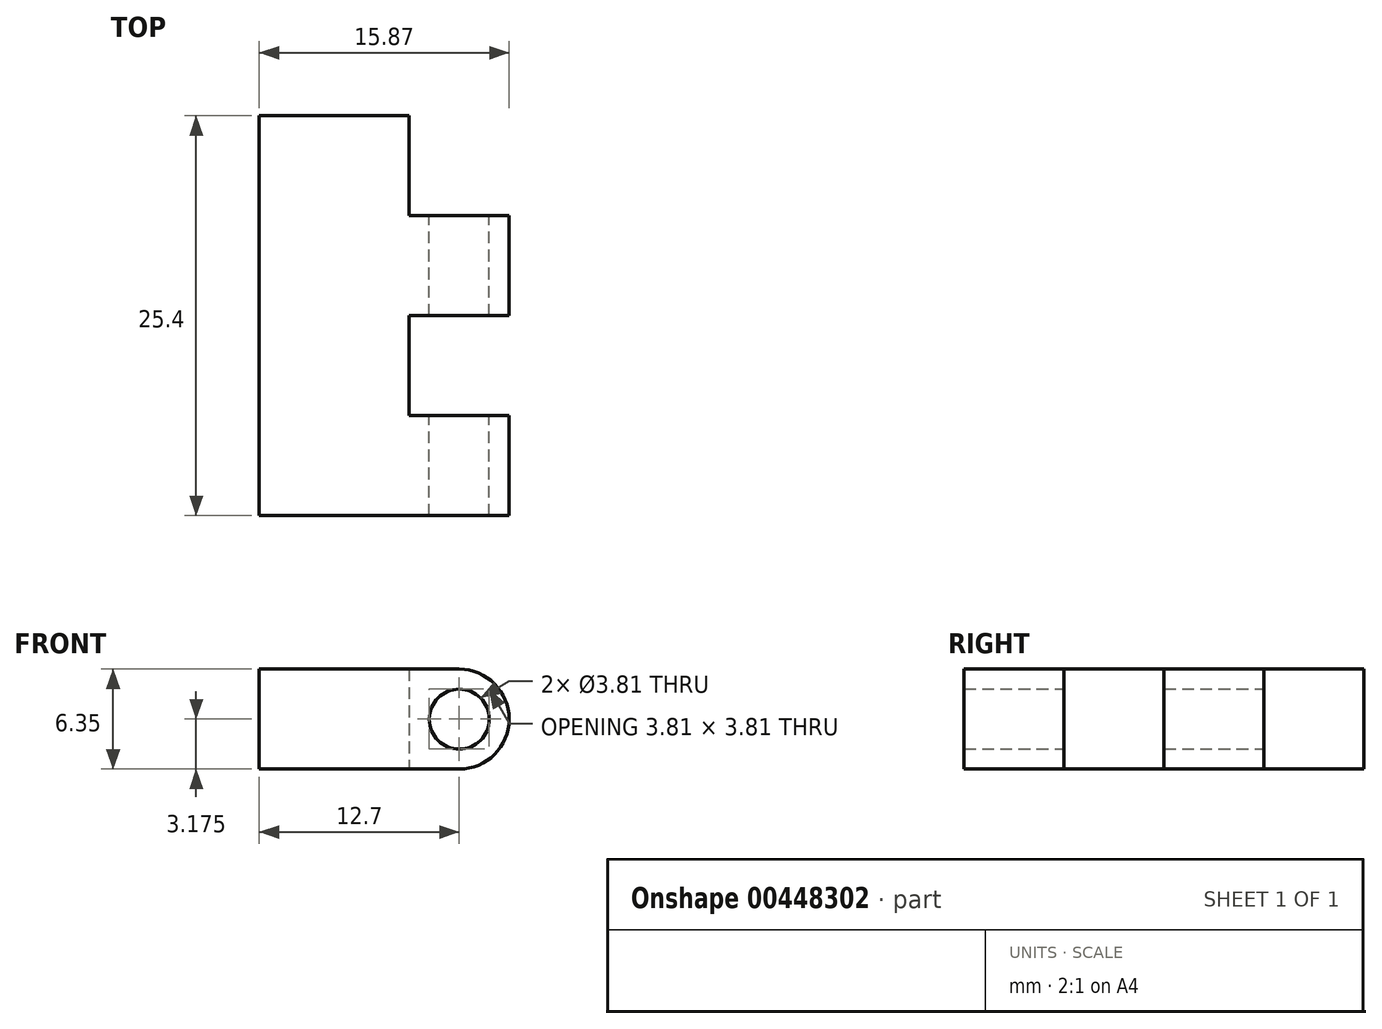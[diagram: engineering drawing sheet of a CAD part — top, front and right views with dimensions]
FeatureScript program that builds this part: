
annotation { "Feature Type Name" : "Feature", "Feature Type Description" : "" }
export const myFeature = defineFeature(function(context is Context, id is Id, definition is map)
    precondition{}
    {
        {
            var Q0;
            Q0=qCreatedBy(makeId("Top.planeOp"),FACE);
            var sketch = newSketch(context, id + "F0", { "sketchPlane" : qUnion([Q0])});
            skLineSegment(sketch, "E0.bottom", {"start": v(6.35, -12.7) * mm, "end": v(-6.35, -12.7) * mm});
            skLineSegment(sketch, "E0.top", {"start": v(6.35, 12.7) * mm, "end": v(-6.35, 12.7) * mm});
            skLineSegment(sketch, "E0.left", {"start": v(6.35, -12.7) * mm, "end": v(6.35, 12.7) * mm});
            skLineSegment(sketch, "E0.right", {"start": v(-6.35, -12.7) * mm, "end": v(-6.35, 12.7) * mm});
            skPoint(sketch, "E0.middle", {"position": v(0, 0) * mm});
            skSolve(sketch);
        }
        {
            var Q0;
            Q0 = qSketchRegion(id + "F0", true);
            extrude(context, id + "F1", {"entities" : qUnion([Q0]), "depth" : 6.35 * mm});
        }
        {
            var Q0;
            Q0=makeQuery(id+"F1.opExtrude","SWEPT_FACE",FACE,{"disambiguationData":[OSD([sQuery(id+"F0.wireOp",EDGE,"E0.top")])]});
            var sketch = newSketch(context, id + "F2", { "sketchPlane" : qUnion([Q0])});
            skCircle(sketch, "E1", {"center": v(-6.35, 3.18) * mm, "radius": 3.17 * mm});
            skCircle(sketch, "E2", {"center": v(-6.35, 3.18) * mm, "radius": 1.9 * mm});
            skSolve(sketch);
        }
        {
            var Q0;
            Q0 = qSketchRegion(id + "F2", true);
            var Q1;
            {var subQ0=sQuery(id+"F2.wireOp",EDGE,"E2");var subQ1=makeQuery(id+"F1.opExtrude","SWEPT_EDGE",EDGE,{"disambiguationData":[OSD([sQuery(id+"F0.wireOp",EDGE,"E0.top"),sQuery(id+"F0.wireOp",EDGE,"E0.left")])]});var subQ2=makeQuery(id+"F2.imprint","INTERSECT",VERTEX,{"disambiguationData":[OD(0.0)],"derivedFrom":[subQ1,subQ0]});Q1=makeQuery(id+"F2.imprint","IMPRINT",FACE,{"disambiguationData":[TD([[makeQuery(id+"F2.imprint","IMPRINT",EDGE,{"disambiguationData":[TD([[subQ2,1.0]])],"derivedFrom":subQ0}),1.0]])]});}
            extrude(context, id + "F3", {"entities" : qUnion([Q0, Q1]), "operationType" : NewBodyOperationType.ADD, "oppositeDirection" : true, "depth" : 25.4 * mm});
        }
        {
            var Q0;
            {var subQ0=sQuery(id+"F2.wireOp",EDGE,"E2");var subQ1=makeQuery(id+"F1.opExtrude","SWEPT_EDGE",EDGE,{"disambiguationData":[OSD([sQuery(id+"F0.wireOp",EDGE,"E0.top"),sQuery(id+"F0.wireOp",EDGE,"E0.left")])]});var subQ2=makeQuery(id+"F2.imprint","INTERSECT",VERTEX,{"disambiguationData":[OD(0.0)],"derivedFrom":[subQ1,subQ0]});Q0=makeQuery(id+"F2.imprint","IMPRINT",FACE,{"disambiguationData":[TD([[makeQuery(id+"F2.imprint","IMPRINT",EDGE,{"disambiguationData":[TD([[subQ2,1.0]])],"derivedFrom":subQ0}),1.0]])]});}
            var Q1;
            {var subQ0=sQuery(id+"F2.wireOp",EDGE,"E2");var subQ1=makeQuery(id+"F1.opExtrude","SWEPT_EDGE",EDGE,{"disambiguationData":[OSD([sQuery(id+"F0.wireOp",EDGE,"E0.top"),sQuery(id+"F0.wireOp",EDGE,"E0.left")])]});var subQ2=makeQuery(id+"F2.imprint","INTERSECT",VERTEX,{"disambiguationData":[OD(0.0)],"derivedFrom":[subQ1,subQ0]});Q1=makeQuery(id+"F2.imprint","IMPRINT",FACE,{"disambiguationData":[TD([[makeQuery(id+"F2.imprint","IMPRINT",EDGE,{"disambiguationData":[TD([[subQ2,-1.0]])],"derivedFrom":subQ0}),1.0]])]});}
            extrude(context, id + "F4", {"entities" : qUnion([Q0, Q1]), "operationType" : NewBodyOperationType.REMOVE, "oppositeDirection" : true, "depth" : 25.4 * mm});
        }
        {
            var Q0;
            Q0=makeQuery(id+"F1.opExtrude","CAP_FACE",FACE,{"disambiguationData":[OSD([sQuery(id+"F0.wireOp",EDGE,"E0.bottom"),sQuery(id+"F0.wireOp",EDGE,"E0.top"),sQuery(id+"F0.wireOp",EDGE,"E0.left"),sQuery(id+"F0.wireOp",EDGE,"E0.right")])],"isStart":true});
            var sketch = newSketch(context, id + "F5", { "sketchPlane" : qUnion([Q0])});
            skPoint(sketch, "E3.middle", {"position": v(6.35, 9.52) * mm});
            skLineSegment(sketch, "E4.MirrorCS", {"start": v(3.18, -12.7) * mm, "end": v(3.18, -6.35) * mm});
            skLineSegment(sketch, "E5.MirrorCS", {"start": v(9.53, -12.7) * mm, "end": v(9.53, -6.35) * mm});
            skLineSegment(sketch, "E6.MirrorCS", {"start": v(9.52, -12.7) * mm, "end": v(3.18, -12.7) * mm});
            skLineSegment(sketch, "E7", {"start": v(3.18, -6.35) * mm, "end": v(9.53, -6.35) * mm});
            skPoint(sketch, "E8.firstSnap0", {"position": v(6.35, 0) * mm});
            skLineSegment(sketch, "E8.bottom", {"start": v(9.53, 0) * mm, "end": v(3.18, 0) * mm});
            skLineSegment(sketch, "E8.top", {"start": v(9.53, 6.35) * mm, "end": v(3.18, 6.35) * mm});
            skLineSegment(sketch, "E8.left", {"start": v(9.53, 0) * mm, "end": v(9.53, 6.35) * mm});
            skLineSegment(sketch, "E8.right", {"start": v(3.18, 0) * mm, "end": v(3.18, 6.35) * mm});
            skLineSegment(sketch, "E9.top", {"start": v(3.18, -12.7) * mm, "end": v(9.53, -12.7) * mm});
            skLineSegment(sketch, "E9.left", {"start": v(3.18, -6.35) * mm, "end": v(3.18, -12.7) * mm});
            skLineSegment(sketch, "E9.right", {"start": v(9.53, -6.35) * mm, "end": v(9.53, -12.7) * mm});
            skSolve(sketch);
        }
        {
            var Q0;
            Q0 = qSketchRegion(id + "F5", true);
            extrude(context, id + "F6", {"entities" : qUnion([Q0]), "operationType" : NewBodyOperationType.REMOVE, "oppositeDirection" : true, "depth" : 25.4 * mm});
        }
    });
